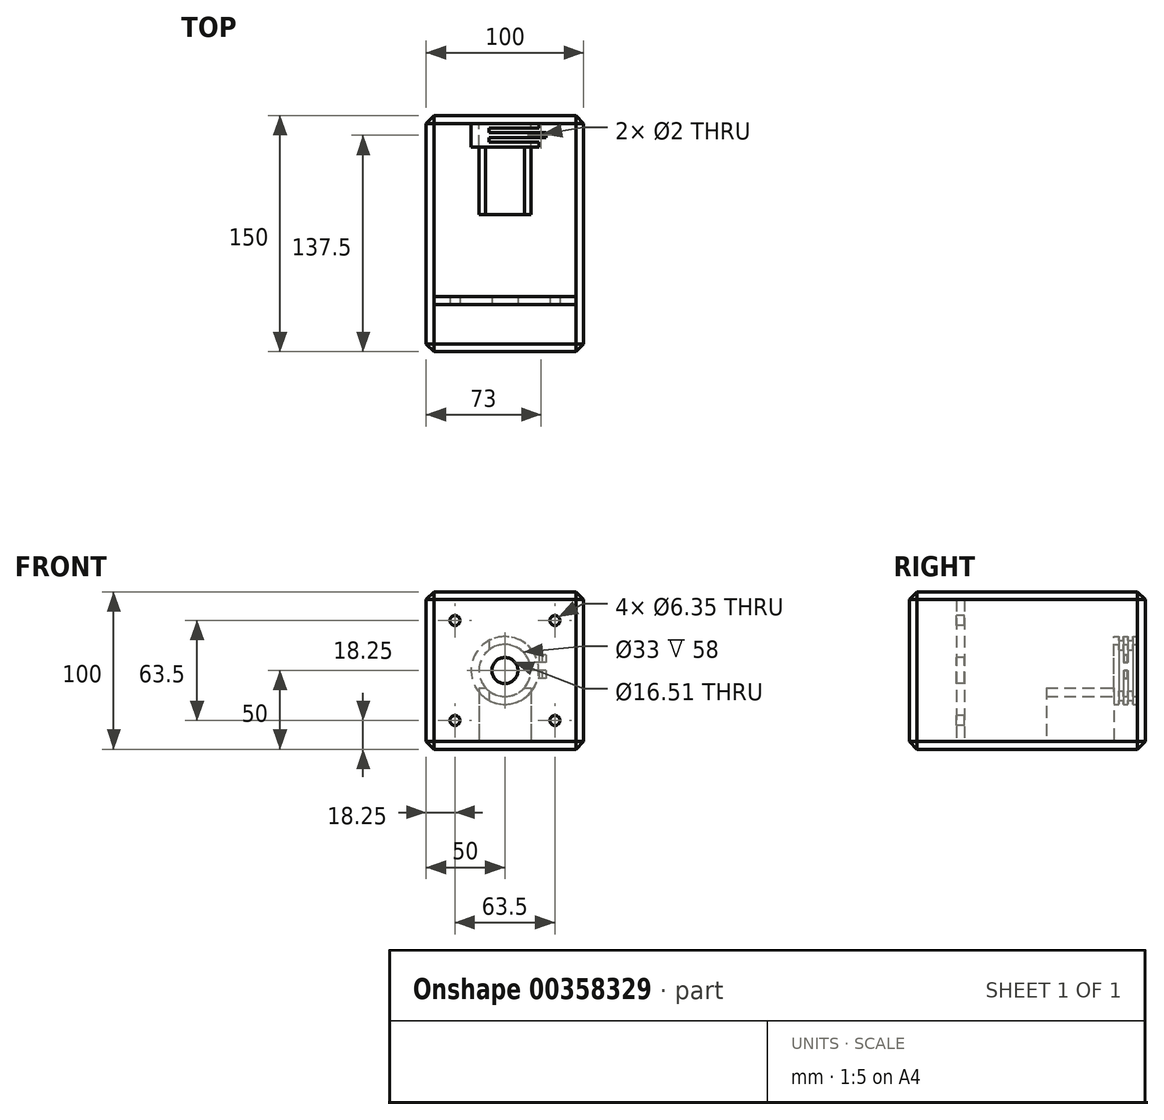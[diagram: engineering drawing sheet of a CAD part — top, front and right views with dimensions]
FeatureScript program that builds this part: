
annotation { "Feature Type Name" : "Feature", "Feature Type Description" : "" }
export const myFeature = defineFeature(function(context is Context, id is Id, definition is map)
    precondition{}
    {
        {
            var Q0;
            Q0=qCreatedBy(makeId("Front.planeOp"),FACE);
            var sketch = newSketch(context, id + "F0", { "sketchPlane" : qUnion([Q0])});
            skLineSegment(sketch, "E0.bottom", {"start": v(50, -50) * mm, "end": v(-50, -50) * mm});
            skLineSegment(sketch, "E0.top", {"start": v(50, 50) * mm, "end": v(-50, 50) * mm});
            skLineSegment(sketch, "E0.left", {"start": v(50, -50) * mm, "end": v(50, 50) * mm});
            skLineSegment(sketch, "E0.right", {"start": v(-50, -50) * mm, "end": v(-50, 50) * mm});
            skPoint(sketch, "E0.middle", {"position": v(0, 0) * mm});
            skSolve(sketch);
        }
        {
            var Q0;
            Q0 = qSketchRegion(id + "F0", true);
            extrude(context, id + "F1", {"entities" : qUnion([Q0]), "depth" : 150 * mm});
        }
        {
            var Q0;
            Q0=makeQuery(id+"F1.opExtrude","CAP_FACE",FACE,{"disambiguationData":[OSD([sQuery(id+"F0.wireOp",EDGE,"E0.bottom"),sQuery(id+"F0.wireOp",EDGE,"E0.top"),sQuery(id+"F0.wireOp",EDGE,"E0.left"),sQuery(id+"F0.wireOp",EDGE,"E0.right")])],"isStart":false});
            var sketch = newSketch(context, id + "F2", { "sketchPlane" : qUnion([Q0])});
            skLineSegment(sketch, "E1.bottom", {"start": v(45, -45) * mm, "end": v(-45, -45) * mm});
            skLineSegment(sketch, "E1.top", {"start": v(45, 45) * mm, "end": v(-45, 45) * mm});
            skLineSegment(sketch, "E1.left", {"start": v(45, -45) * mm, "end": v(45, 45) * mm});
            skLineSegment(sketch, "E1.right", {"start": v(-45, -45) * mm, "end": v(-45, 45) * mm});
            skPoint(sketch, "E1.middle", {"position": v(0, 0) * mm});
            skSolve(sketch);
        }
        {
            var Q0;
            Q0 = qSketchRegion(id + "F2", true);
            extrude(context, id + "F3", {"entities" : qUnion([Q0]), "operationType" : NewBodyOperationType.REMOVE, "oppositeDirection" : true, "depth" : 145 * mm});
        }
        {
            var Q0;
            Q0=makeQuery(id+"F1.opExtrude","CAP_FACE",FACE,{"disambiguationData":[OSD([sQuery(id+"F0.wireOp",EDGE,"E0.bottom"),sQuery(id+"F0.wireOp",EDGE,"E0.top"),sQuery(id+"F0.wireOp",EDGE,"E0.left"),sQuery(id+"F0.wireOp",EDGE,"E0.right")])],"isStart":true});
            var sketch = newSketch(context, id + "F4", { "sketchPlane" : qUnion([Q0])});
            skCircle(sketch, "E2", {"center": v(0, 0) * mm, "radius": 7.94 * mm});
            skSolve(sketch);
        }
        {
            var Q0;
            Q0=makeQuery(id+"F3.boolean.opBoolean","COPY",FACE,{"derivedFrom":makeQuery(id+"F3.opExtrude","CAP_FACE",FACE,{"disambiguationData":[OSD([sQuery(id+"F2.wireOp",EDGE,"E1.bottom"),sQuery(id+"F2.wireOp",EDGE,"E1.top"),sQuery(id+"F2.wireOp",EDGE,"E1.left"),sQuery(id+"F2.wireOp",EDGE,"E1.right")])],"isStart":false})});
            var sketch = newSketch(context, id + "F5", { "sketchPlane" : qUnion([Q0])});
            skCircle(sketch, "E3", {"center": v(0, 0) * mm, "radius": 16.5 * mm});
            skCircle(sketch, "E4", {"center": v(0, 0) * mm, "radius": 21.5 * mm});
            skSolve(sketch);
        }
        {
            var Q0;
            Q0 = qSketchRegion(id + "F5", true);
            extrude(context, id + "F6", {"entities" : qUnion([Q0]), "operationType" : NewBodyOperationType.ADD, "depth" : 15 * mm});
        }
        {
            var Q0;
            Q0=qCreatedBy(makeId("Right.planeOp"),FACE);
            var sketch = newSketch(context, id + "F7", { "sketchPlane" : qUnion([Q0])});
            skLineSegment(sketch, "E5.bottom", {"start": v(-11, 21.5) * mm, "end": v(-8, 21.5) * mm});
            skLineSegment(sketch, "E5.top", {"start": v(-11, -21.5) * mm, "end": v(-8, -21.5) * mm});
            skLineSegment(sketch, "E5.left", {"start": v(-11, 21.5) * mm, "end": v(-11, 5) * mm});
            skLineSegment(sketch, "E5.right", {"start": v(-8, 21.5) * mm, "end": v(-8, -21.5) * mm});
            skLineSegment(sketch, "E6.bottom", {"start": v(-17, 21.5) * mm, "end": v(-14, 21.5) * mm});
            skLineSegment(sketch, "E6.top", {"start": v(-17, -21.5) * mm, "end": v(-14, -21.5) * mm});
            skLineSegment(sketch, "E6.left", {"start": v(-17, 21.5) * mm, "end": v(-17, -21.5) * mm});
            skLineSegment(sketch, "E6.right", {"start": v(-14, 21.5) * mm, "end": v(-14, 5) * mm});
            skLineSegment(sketch, "E7", {"start": v(-14, 0) * mm, "end": v(-11, 0) * mm});
            skLineSegment(sketch, "E8", {"start": v(-14, 5) * mm, "end": v(-11, 5) * mm});
            skLineSegment(sketch, "E9.trimOffspring", {"start": v(-14, 0) * mm, "end": v(-14, -21.5) * mm});
            skLineSegment(sketch, "E10.trimOffspring", {"start": v(-11, 0) * mm, "end": v(-11, -21.5) * mm});
            skSolve(sketch);
        }
        {
            var Q0;
            Q0 = qSketchRegion(id + "F7", true);
            extrude(context, id + "F8", {"entities" : qUnion([Q0]), "operationType" : NewBodyOperationType.REMOVE, "depth" : 21.7 * mm, "hasSecondDirection" : true, "secondDirectionOppositeDirection" : true, "secondDirectionDepth" : 10 * mm});
        }
        {
            var Q0;
            Q0=qCreatedBy(makeId("Right.planeOp"),FACE);
            cPlane(context, id + "F9", {"entities" : qUnion([Q0]), "cplaneType" : CPlaneType.OFFSET, "offset" : 21 * mm, "width" : 150 * mm, "height" : 150 * mm});
        }
        {
            var Q0;
            Q0=qCreatedBy(id+"F9.planeOp",FACE);
            var sketch = newSketch(context, id + "F10", { "sketchPlane" : qUnion([Q0])});
            skLineSegment(sketch, "E11.bottom", {"start": v(-14, 10) * mm, "end": v(-11, 10) * mm});
            skLineSegment(sketch, "E11.top", {"start": v(-14, 5) * mm, "end": v(-11, 5) * mm});
            skLineSegment(sketch, "E11.left", {"start": v(-14, 10) * mm, "end": v(-14, 5) * mm});
            skLineSegment(sketch, "E11.right", {"start": v(-11, 10) * mm, "end": v(-11, 5) * mm});
            skLineSegment(sketch, "E12.bottom", {"start": v(-14, 0) * mm, "end": v(-11, 0) * mm});
            skLineSegment(sketch, "E12.top", {"start": v(-14, -5) * mm, "end": v(-11, -5) * mm});
            skLineSegment(sketch, "E12.left", {"start": v(-14, 0) * mm, "end": v(-14, -5) * mm});
            skLineSegment(sketch, "E12.right", {"start": v(-11, 0) * mm, "end": v(-11, -5) * mm});
            skSolve(sketch);
        }
        {
            var Q0;
            Q0 = qSketchRegion(id + "F10", true);
            extrude(context, id + "F11", {"entities" : qUnion([Q0]), "operationType" : NewBodyOperationType.ADD, "depth" : 5 * mm, "hasSecondDirection" : true, "secondDirectionOppositeDirection" : true, "secondDirectionDepth" : 4 * mm});
        }
        {
            var Q0;
            Q0=makeQuery(id+"F11.opExtrude","SWEPT_FACE",FACE,{"disambiguationData":[OSD([sQuery(id+"F10.wireOp",EDGE,"E11.bottom")])]});
            var sketch = newSketch(context, id + "F12", { "sketchPlane" : qUnion([Q0])});
            skCircle(sketch, "E13", {"center": v(23, -12.5) * mm, "radius": 1 * mm});
            skSolve(sketch);
        }
        {
            var Q0;
            Q0 = qSketchRegion(id + "F12", true);
            var Q1;
            Q1=makeQuery(id+"F11.opExtrude","SWEPT_FACE",FACE,{"disambiguationData":[OSD([sQuery(id+"F10.wireOp",EDGE,"E12.top")])]});
            extrude(context, id + "F13", {"entities" : qUnion([Q0]), "operationType" : NewBodyOperationType.REMOVE, "endBound" : BoundingType.UP_TO_SURFACE, "oppositeDirection" : true, "endBoundEntityFace" : qUnion([Q1]), "depth" : 25 * mm});
        }
        {
            var Q0;
            Q0=makeQuery(id+"F3.boolean.opBoolean","COPY",FACE,{"derivedFrom":makeQuery(id+"F3.opExtrude","SWEPT_FACE",FACE,{"disambiguationData":[OSD([sQuery(id+"F2.wireOp",EDGE,"E1.bottom")])]})});
            var sketch = newSketch(context, id + "F14", { "sketchPlane" : qUnion([Q0])});
            skLineSegment(sketch, "E14.bottom", {"start": v(-16.5, -20) * mm, "end": v(16.5, -20) * mm});
            skLineSegment(sketch, "E14.top", {"start": v(-16.5, -63) * mm, "end": v(16.5, -63) * mm});
            skLineSegment(sketch, "E14.left", {"start": v(-16.5, -20) * mm, "end": v(-16.5, -63) * mm});
            skLineSegment(sketch, "E14.right", {"start": v(16.5, -20) * mm, "end": v(16.5, -63) * mm});
            skPoint(sketch, "E15", {"position": v(0, -20) * mm});
            skSolve(sketch);
        }
        {
            var Q0;
            Q0 = qSketchRegion(id + "F14", true);
            extrude(context, id + "F15", {"entities" : qUnion([Q0]), "operationType" : NewBodyOperationType.ADD, "depth" : 34 * mm});
        }
        {
            var Q0;
            {var subQ0=sQuery(id+"F5.wireOp",EDGE,"E3");var subQ1=sQuery(id+"F14.wireOp",EDGE,"E14.bottom");Q0=makeQuery(id+"F15.boolean.opBoolean","SPLIT",FACE,{"disambiguationData":[TD([makeQuery(id+"F6.opExtrude","SWEPT_FACE",FACE,{"disambiguationData":[OSD([subQ0])]})])],"derivedFrom":makeQuery(id+"F15.opExtrude","SWEPT_FACE",FACE,{"disambiguationData":[OSD([subQ1])]})});}
            var sketch = newSketch(context, id + "F16", { "sketchPlane" : qUnion([Q0])});
            skLineSegment(sketch, "E16", {"start": v(-12.3, -11) * mm, "end": v(12.3, -11) * mm});
            skArc(sketch, "E17", {"start": v(-12.3, -11) * mm, "mid": v(0, -16.5) * mm, "end": v(12.3, -11) * mm});
            skSolve(sketch);
        }
        {
            var Q0;
            Q0 = qSketchRegion(id + "F16", true);
            extrude(context, id + "F17", {"entities" : qUnion([Q0]), "operationType" : NewBodyOperationType.REMOVE, "endBound" : BoundingType.THROUGH_ALL, "oppositeDirection" : true, "depth" : 25 * mm});
        }
        {
            var Q0;
            Q0=makeQuery(id+"F1.opExtrude","SWEPT_FACE",FACE,{"disambiguationData":[OSD([sQuery(id+"F0.wireOp",EDGE,"E0.top")])]});
            var Q1;
            Q1=makeQuery(id+"F1.opExtrude","SWEPT_FACE",FACE,{"disambiguationData":[OSD([sQuery(id+"F0.wireOp",EDGE,"E0.left")])]});
            var Q2;
            Q2=makeQuery(id+"F1.opExtrude","SWEPT_FACE",FACE,{"disambiguationData":[OSD([sQuery(id+"F0.wireOp",EDGE,"E0.bottom")])]});
            var Q3;
            Q3=makeQuery(id+"F1.opExtrude","SWEPT_FACE",FACE,{"disambiguationData":[OSD([sQuery(id+"F0.wireOp",EDGE,"E0.right")])]});
            chamfer(context, id + "F18", {"entities" : qUnion([Q0, Q1, Q2, Q3]), "width" : 5 * mm, "tangentPropagation" : true});
        }
        {
            var Q0;
            Q0=makeQuery(id+"F3.boolean.opBoolean","COPY",FACE,{"derivedFrom":makeQuery(id+"F3.opExtrude","SWEPT_FACE",FACE,{"disambiguationData":[OSD([sQuery(id+"F2.wireOp",EDGE,"E1.bottom")])]})});
            var sketch = newSketch(context, id + "F19", { "sketchPlane" : qUnion([Q0])});
            skLineSegment(sketch, "E18.bottom", {"start": v(-45, -120) * mm, "end": v(45, -120) * mm});
            skLineSegment(sketch, "E18.top", {"start": v(-45, -115) * mm, "end": v(45, -115) * mm});
            skLineSegment(sketch, "E18.left", {"start": v(-45, -120) * mm, "end": v(-45, -115) * mm});
            skLineSegment(sketch, "E18.right", {"start": v(45, -120) * mm, "end": v(45, -115) * mm});
            skSolve(sketch);
        }
        {
            var Q0;
            Q0 = qSketchRegion(id + "F19", true);
            var Q1;
            Q1=makeQuery(id+"F3.boolean.opBoolean","COPY",FACE,{"derivedFrom":makeQuery(id+"F3.opExtrude","SWEPT_FACE",FACE,{"disambiguationData":[OSD([sQuery(id+"F2.wireOp",EDGE,"E1.top")])]})});
            extrude(context, id + "F20", {"entities" : qUnion([Q0]), "operationType" : NewBodyOperationType.ADD, "endBound" : BoundingType.UP_TO_SURFACE, "endBoundEntityFace" : qUnion([Q1]), "depth" : 25 * mm});
        }
        {
            var Q0;
            Q0=makeQuery(id+"F20.opExtrude","SWEPT_FACE",FACE,{"disambiguationData":[OSD([sQuery(id+"F19.wireOp",EDGE,"E18.bottom")])]});
            var sketch = newSketch(context, id + "F21", { "sketchPlane" : qUnion([Q0])});
            skCircle(sketch, "E19", {"center": v(0, 0) * mm, "radius": 8.26 * mm});
            skSolve(sketch);
        }
        {
            var Q0;
            Q0 = qSketchRegion(id + "F21", true);
            extrude(context, id + "F22", {"entities" : qUnion([Q0]), "operationType" : NewBodyOperationType.REMOVE, "oppositeDirection" : true, "depth" : 5 * mm});
        }
        {
            var Q0;
            Q0=makeQuery(id+"F20.opExtrude","SWEPT_FACE",FACE,{"disambiguationData":[OSD([sQuery(id+"F19.wireOp",EDGE,"E18.bottom")])]});
            var sketch = newSketch(context, id + "F23", { "sketchPlane" : qUnion([Q0])});
            skCircle(sketch, "E20", {"center": v(-31.75, 31.75) * mm, "radius": 3.18 * mm});
            skCircle(sketch, "E21.0.1.0", {"center": v(-31.75, -31.75) * mm, "radius": 3.18 * mm});
            skCircle(sketch, "E21.1.0.0", {"center": v(31.75, 31.75) * mm, "radius": 3.18 * mm});
            skCircle(sketch, "E21.1.1.0", {"center": v(31.75, -31.75) * mm, "radius": 3.18 * mm});
            skLineSegment(sketch, "E21.direction1", {"start": v(-31.75, 31.75) * mm, "end": v(31.75, 31.75) * mm, "construction": true});
            skLineSegment(sketch, "E21.direction2", {"start": v(-31.75, -31.75) * mm, "end": v(-31.75, 31.75) * mm, "construction": true});
            skPoint(sketch, "E22", {"position": v(0, 31.75) * mm});
            skPoint(sketch, "E23", {"position": v(0, 45) * mm});
            skPoint(sketch, "E23.positionSnap0", {"position": v(0, 45) * mm});
            skPoint(sketch, "E24", {"position": v(-31.75, 0) * mm});
            skPoint(sketch, "E25", {"position": v(-45, 0) * mm});
            skSolve(sketch);
        }
        {
            var Q0;
            Q0 = qSketchRegion(id + "F23", true);
            extrude(context, id + "F24", {"entities" : qUnion([Q0]), "operationType" : NewBodyOperationType.REMOVE, "oppositeDirection" : true, "depth" : 5 * mm});
        }
        {
            var Q0;
            Q0=makeQuery(id+"F1.opExtrude","SWEPT_FACE",FACE,{"disambiguationData":[OSD([sQuery(id+"F0.wireOp",EDGE,"E0.top")])]});
            var Q1;
            {var subQ2=sQuery(id+"F2.wireOp",EDGE,"E1.top");Q1=makeQuery(id+"F20.boolean.opBoolean","SPLIT",FACE,{"disambiguationData":[TD([makeQuery(id+"F20.opExtrude","SWEPT_FACE",FACE,{"disambiguationData":[OSD([sQuery(id+"F19.wireOp",EDGE,"E18.top")])]})])],"derivedFrom":makeQuery(id+"F3.boolean.opBoolean","COPY",FACE,{"derivedFrom":makeQuery(id+"F3.opExtrude","SWEPT_FACE",FACE,{"disambiguationData":[OSD([subQ2])]})})});}
            extrude(context, id + "F25", {"entities" : qUnion([Q0]), "operationType" : NewBodyOperationType.REMOVE, "endBound" : BoundingType.UP_TO_SURFACE, "oppositeDirection" : true, "depth" : 25 * mm, "endBoundEntityFace" : qUnion([Q1]), "offsetDistance" : 25 * mm});
        }
    });
